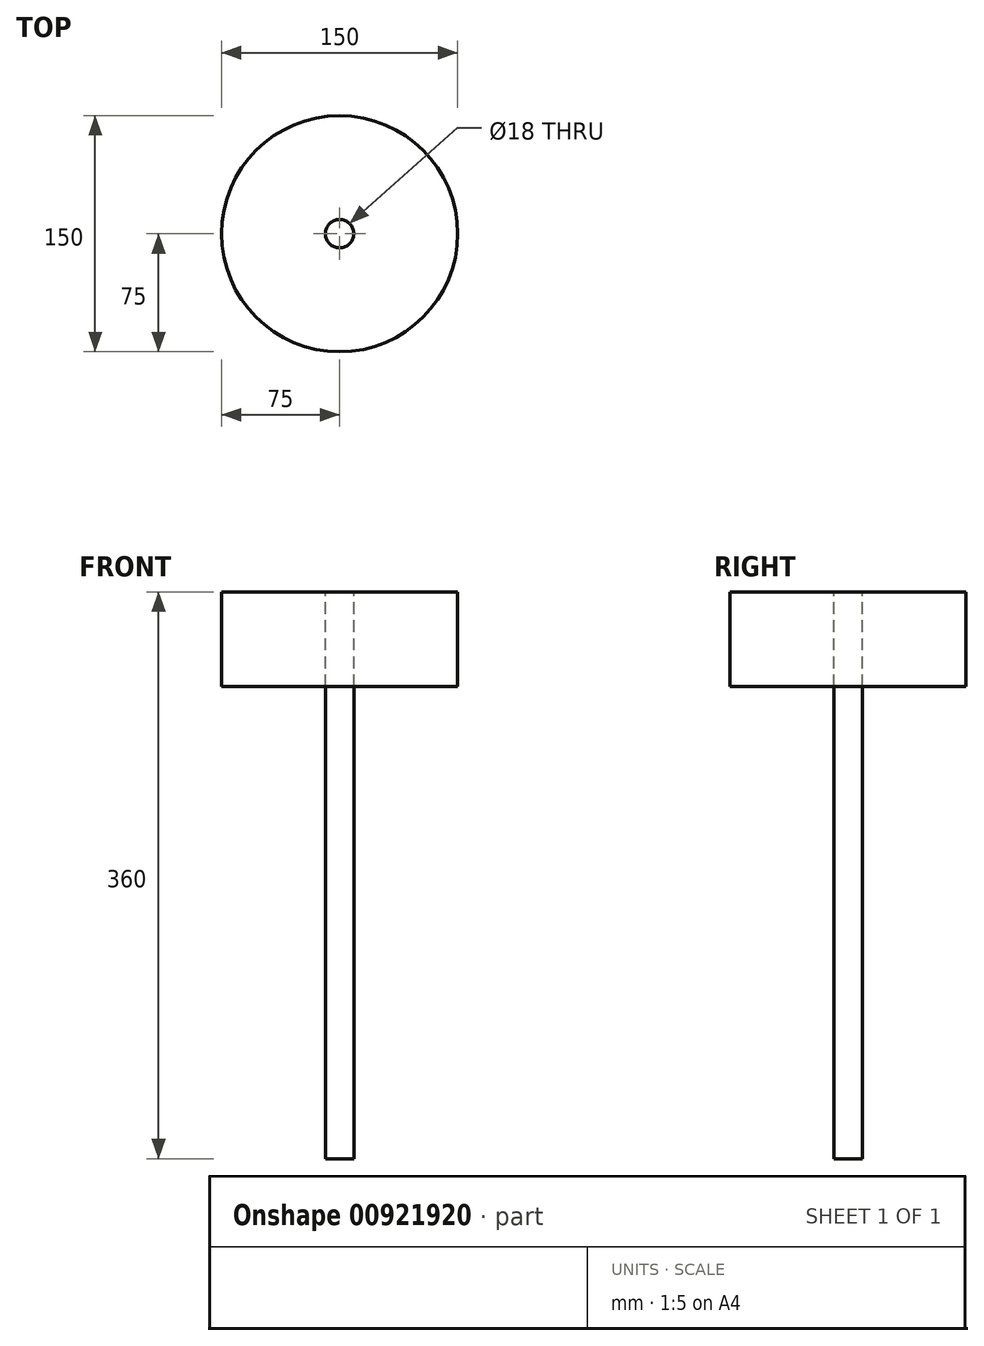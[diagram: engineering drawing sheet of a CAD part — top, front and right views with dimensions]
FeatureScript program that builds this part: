
annotation { "Feature Type Name" : "Feature", "Feature Type Description" : "" }
export const myFeature = defineFeature(function(context is Context, id is Id, definition is map)
    precondition{}
    {
        {
            var Q0;
            Q0=qCreatedBy(makeId("Top.planeOp"),FACE);
            var sketch = newSketch(context, id + "F0", { "sketchPlane" : qUnion([Q0])});
            skCircle(sketch, "E0", {"center": v(0, 0) * mm, "radius": 9 * mm});
            skCircle(sketch, "E1", {"center": v(0, 0) * mm, "radius": 75 * mm});
            skSolve(sketch);
        }
        {
            var Q0;
            Q0=makeQuery(id+"F0.imprint","IMPRINT",FACE,{"disambiguationData":[TD([[makeQuery(id+"F0.imprint","IMPRINT",EDGE,{"derivedFrom":sQuery(id+"F0.wireOp",EDGE,"E0")}),1.0]])]});
            extrude(context, id + "F1", {"entities" : qUnion([Q0]), "depth" : 260 * mm, "offsetDistance" : 25 * mm, "hasSecondDirection" : true, "secondDirectionOppositeDirection" : true, "secondDirectionDepth" : 100 * mm});
        }
        {
            var Q0;
            Q0 = qSketchRegion(id + "F0", true);
            extrude(context, id + "F2", {"entities" : qUnion([Q0]), "oppositeDirection" : true, "depth" : 60 * mm, "offsetDistance" : 25 * mm});
        }
        {
            var Q0;
            Q0=makeQuery(id+"F2.opExtrude","SWEPT_BODY",BODY,{"disambiguationData":[OSD([sQuery(id+"F0.wireOp",EDGE,"E0"),sQuery(id+"F0.wireOp",EDGE,"E1")])]});
            transform(context, id + "F3", {"entities" : qUnion([Q0]), "transformType" : TransformType.TRANSLATION_3D, "dx" : 0 * mm, "dy" : 0 * mm, "dz" : 260 * mm, "makeCopy" : false});
        }
    });
